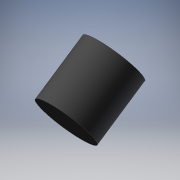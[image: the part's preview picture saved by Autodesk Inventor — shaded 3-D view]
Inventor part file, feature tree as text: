
AUTODESK INVENTOR PART (.ipt)
format: ipt  version: 2019 (Build 230136000, 136)  size: 109,056 bytes
history: native  units: mm
features: extrude x1, sketch x1
ambient origin geometry x8: Origin, YZ Plane, XZ Plane, XY Plane, X Axis, Y Axis, Z Axis, Center Point
bodies: Solid1 (feature_tree)
feature tree (2):
  extrude  "Extrusion1"  [1 undecoded]
  sketch  "Sketch_1"  dims[d0=1.67mm d1=0.0mm]
note: 1 required parameter value undecoded (feature->parameter linkage not recoverable at this tier; creation-order binding heuristic only, values carry confidence <= 0.55)
